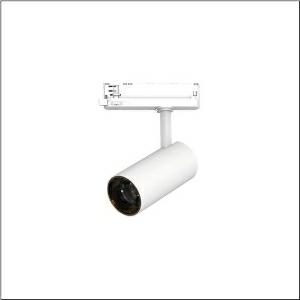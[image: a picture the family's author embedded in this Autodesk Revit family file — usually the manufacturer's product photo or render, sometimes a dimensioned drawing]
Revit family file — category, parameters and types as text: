
# Revit family: spot_31_slim_51sf127fb2b
name_source: partatom
category: Lighting Fixtures
units: mm (PartAtom-declared; Revit-internal decimal feet)

## family parameters
Cut with Voids When Loaded = No
Host = Face
Light Source = No
Part Type = Normal
Room Calculation Point = No
Round Connector Dimension = Use Diameter
Shared = No

## types (1)
- Spot 31 Slim (1 x LED, 1970 lm, 16.2 W, 3000K)
    Apparent Load = 16 VA
    CIE Flux Codes = 94 98 99 100 100
    Color Rendering = 90
    Color Temperature = 3000K
    Default Elevation = 1800 mm
    Description = Spot 31 Slim, directional spotlight, light control with reflector, of aluminium, LED rated luminous flux: 2.150lm, light colour: 930, control gear: ECG, with 3-phase adapter, mains connection: 220..240V, AC, 50/60Hz, housing, of aluminium, traffic white (RAL 9016), diameter: 70mm, adapter, of plastic, protection rating (complete): IP20, insulation class (complete): insulation class I (protective earthing), certification: CE, impact resistance: IK02, packaging unit: 1 piece
    Height = 210 mm
    Lamp = 1 x LED
    Lamp Light Flux = 1970 lm
    Lamp Power = 16.2 W
    Lamp count = 1
    Length = 70 mm
    Luminous efficacy = 122 lm/W
    Manufacturer = Siteco
    ModVariant = No
    Model = 51SF127FB2B
    Mounting Place = Ceiling
    Mounting Type = Pendant
    Number of Poles = 1
    OnlyDefault = Yes
    Power Factor = 1
    Product Name = Spot 31 Slim
    Product group = directional spotlight
    ProductGroupID = 906
    Protection Class = Protection class I
    Protection Degree = IP 20
    RLX_Detail_Level = 1
    RLX_Emergency_Light_Flux = 0 lm
    RLX_Emergency_Type = 0
    RLX_Emergency_Type_DB = No
    RlxData = <blob elided: 14165 chars, md5=7c45882c>
    Socket = socket
    Standby Power = 0 W
    System Light Flux = 1970 lm
    System Power = 16 W
    Type Comments = Product without accessories
    Type Image = l_1228468.jpg
    URL = http://relux.com
    VarID = ---
    Voltage = 0 V
    Weight = 0.00 kg
    Width = 0 mm  [stored 0 ft]

note: [stored X ft] marks values corroborated as IEEE doubles in the binary element streams (Revit-internal decimal feet)

## geometry (parser evidence)
native form markers: Sweep x12
no freeform markers — native parametric forms only
